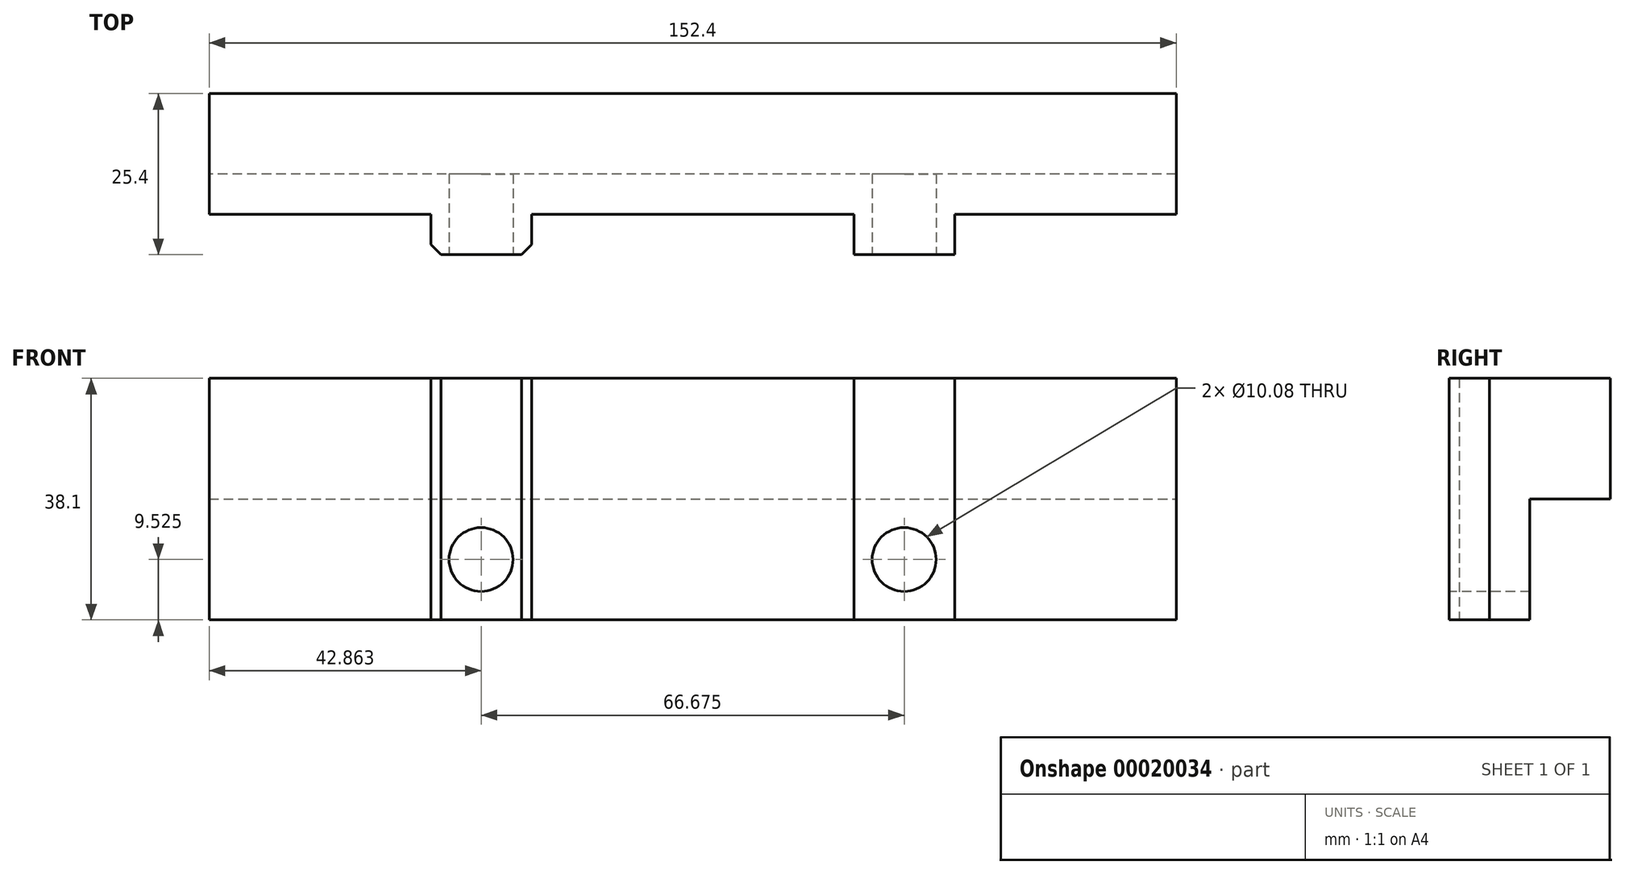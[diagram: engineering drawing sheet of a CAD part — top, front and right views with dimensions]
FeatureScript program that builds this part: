
annotation { "Feature Type Name" : "Feature", "Feature Type Description" : "" }
export const myFeature = defineFeature(function(context is Context, id is Id, definition is map)
    precondition{}
    {
        {
            var Q0;
            Q0=qCreatedBy(makeId("Front.planeOp"),FACE);
            var sketch = newSketch(context, id + "F0", { "sketchPlane" : qUnion([Q0])});
            skLineSegment(sketch, "E0.rect.bottom", {"start": v(76.2, 19.05) * mm, "end": v(-76.2, 19.05) * mm});
            skLineSegment(sketch, "E0.rect.top", {"start": v(76.2, -19.05) * mm, "end": v(-76.2, -19.05) * mm});
            skLineSegment(sketch, "E0.rect.left", {"start": v(76.2, 19.05) * mm, "end": v(76.2, -19.05) * mm});
            skLineSegment(sketch, "E0.rect.right", {"start": v(-76.2, 19.05) * mm, "end": v(-76.2, -19.05) * mm});
            skPoint(sketch, "E0.rect.middle", {"position": v(0, 0) * mm});
            skSolve(sketch);
        }
        {
            var Q0;
            Q0 = qSketchRegion(id + "F0", true);
            extrude(context, id + "F1", {"entities" : qUnion([Q0]), "depth" : 25.4 * mm});
        }
        {
            var Q0;
            Q0=makeQuery(id+"F1.opExtrude","CAP_FACE",FACE,{"disambiguationData":[OSD([sQuery(id+"F0.wireOp",EDGE,"E0.rect.bottom"),sQuery(id+"F0.wireOp",EDGE,"E0.rect.top"),sQuery(id+"F0.wireOp",EDGE,"E0.rect.left"),sQuery(id+"F0.wireOp",EDGE,"E0.rect.right")])],"isStart":false});
            var sketch = newSketch(context, id + "F2", { "sketchPlane" : qUnion([Q0])});
            skLineSegment(sketch, "E1.bottom", {"start": v(-76.2, 19.05) * mm, "end": v(-41.28, 19.05) * mm});
            skLineSegment(sketch, "E1.top", {"start": v(-76.2, -19.05) * mm, "end": v(-41.28, -19.05) * mm});
            skLineSegment(sketch, "E1.left", {"start": v(-76.2, 19.05) * mm, "end": v(-76.2, -19.05) * mm});
            skLineSegment(sketch, "E1.right", {"start": v(-41.28, 19.05) * mm, "end": v(-41.28, -19.05) * mm});
            skLineSegment(sketch, "E2.bottom", {"start": v(-25.4, 19.05) * mm, "end": v(25.4, 19.05) * mm});
            skLineSegment(sketch, "E2.top", {"start": v(-25.4, -19.05) * mm, "end": v(25.4, -19.05) * mm});
            skLineSegment(sketch, "E2.left", {"start": v(-25.4, 19.05) * mm, "end": v(-25.4, -19.05) * mm});
            skLineSegment(sketch, "E2.right", {"start": v(25.4, 19.05) * mm, "end": v(25.4, -19.05) * mm});
            skLineSegment(sketch, "E3.bottom", {"start": v(41.28, 19.05) * mm, "end": v(76.2, 19.05) * mm});
            skLineSegment(sketch, "E3.top", {"start": v(41.28, -19.05) * mm, "end": v(76.2, -19.05) * mm});
            skLineSegment(sketch, "E3.left", {"start": v(41.28, 19.05) * mm, "end": v(41.28, -19.05) * mm});
            skLineSegment(sketch, "E3.right", {"start": v(76.2, 19.05) * mm, "end": v(76.2, -19.05) * mm});
            skSolve(sketch);
        }
        {
            var Q0;
            Q0=makeQuery(id+"F2.imprint","IMPRINT",FACE,{"disambiguationData":[TD([[makeQuery(id+"F2.imprint","IMPRINT",EDGE,{"derivedFrom":sQuery(id+"F2.wireOp",EDGE,"E1.bottom")}),1.0]])]});
            var Q1;
            Q1=makeQuery(id+"F2.imprint","IMPRINT",FACE,{"disambiguationData":[TD([[makeQuery(id+"F2.imprint","IMPRINT",EDGE,{"derivedFrom":sQuery(id+"F2.wireOp",EDGE,"E3.bottom")}),1.0]])]});
            var Q2;
            Q2=makeQuery(id+"F2.imprint","IMPRINT",FACE,{"disambiguationData":[TD([[makeQuery(id+"F2.imprint","IMPRINT",EDGE,{"derivedFrom":sQuery(id+"F2.wireOp",EDGE,"E2.bottom")}),1.0]])]});
            extrude(context, id + "F3", {"entities" : qUnion([Q0, Q1, Q2]), "operationType" : NewBodyOperationType.REMOVE, "oppositeDirection" : true, "depth" : 6.35 * mm});
        }
        {
            var Q0;
            Q0=makeQuery(id+"F3.boolean.opBoolean","COPY",EDGE,{"derivedFrom":makeQuery(id+"F3.opExtrude","CAP_EDGE",EDGE,{"disambiguationData":[OSD([sQuery(id+"F2.wireOp",EDGE,"E1.right")])],"isStart":true})});
            var Q1;
            Q1=makeQuery(id+"F3.boolean.opBoolean","COPY",EDGE,{"derivedFrom":makeQuery(id+"F3.opExtrude","CAP_EDGE",EDGE,{"disambiguationData":[OSD([sQuery(id+"F2.wireOp",EDGE,"E2.left")])],"isStart":true})});
            var Q2;
            Q2=makeQuery(id+"F3.boolean.opBoolean","COPY",EDGE,{"derivedFrom":makeQuery(id+"F3.opExtrude","CAP_EDGE",EDGE,{"disambiguationData":[OSD([sQuery(id+"F2.wireOp",EDGE,"E2.right")])],"isStart":true})});
            var Q3;
            Q3=makeQuery(id+"F3.boolean.opBoolean","COPY",EDGE,{"derivedFrom":makeQuery(id+"F3.opExtrude","CAP_EDGE",EDGE,{"disambiguationData":[OSD([sQuery(id+"F2.wireOp",EDGE,"E3.left")])],"isStart":true})});
            chamfer(context, id + "F4", {"entities" : qUnion([Q0, Q1, Q2, Q3]), "width" : 1.59 * mm, "tangentPropagation" : true});
        }
        {
            var Q0;
            Q0=makeQuery(id+"F1.opExtrude","CAP_FACE",FACE,{"disambiguationData":[OSD([sQuery(id+"F0.wireOp",EDGE,"E0.rect.bottom"),sQuery(id+"F0.wireOp",EDGE,"E0.rect.top"),sQuery(id+"F0.wireOp",EDGE,"E0.rect.left"),sQuery(id+"F0.wireOp",EDGE,"E0.rect.right")])],"isStart":true});
            var sketch = newSketch(context, id + "F5", { "sketchPlane" : qUnion([Q0])});
            skLineSegment(sketch, "E4.bottom", {"start": v(76.2, -19.05) * mm, "end": v(-76.2, -19.05) * mm});
            skLineSegment(sketch, "E4.top", {"start": v(76.2, 0) * mm, "end": v(-76.2, 0) * mm});
            skLineSegment(sketch, "E4.left", {"start": v(76.2, -19.05) * mm, "end": v(76.2, 0) * mm});
            skLineSegment(sketch, "E4.right", {"start": v(-76.2, -19.05) * mm, "end": v(-76.2, 0) * mm});
            skSolve(sketch);
        }
        {
            var Q0;
            Q0 = qSketchRegion(id + "F5", true);
            extrude(context, id + "F6", {"entities" : qUnion([Q0]), "operationType" : NewBodyOperationType.REMOVE, "oppositeDirection" : true, "depth" : 12.7 * mm});
        }
        {
            var Q0;
            {var subQ0=sQuery(id+"F0.wireOp",EDGE,"E0.rect.bottom");var subQ1=sQuery(id+"F0.wireOp",EDGE,"E0.rect.top");Q0=makeQuery(id+"F3.boolean.opBoolean","SPLIT",FACE,{"disambiguationData":[TD([makeQuery(id+"F3.opExtrude","SWEPT_FACE",FACE,{"disambiguationData":[OSD([sQuery(id+"F2.wireOp",EDGE,"E2.right")])]})])],"derivedFrom":makeQuery(id+"F1.opExtrude","CAP_FACE",FACE,{"disambiguationData":[OSD([subQ0,subQ1,sQuery(id+"F0.wireOp",EDGE,"E0.rect.left"),sQuery(id+"F0.wireOp",EDGE,"E0.rect.right")])],"isStart":false})});}
            var sketch = newSketch(context, id + "F7", { "sketchPlane" : qUnion([Q0])});
            skPoint(sketch, "E5", {"position": v(33.34, -9.53) * mm});
            skPoint(sketch, "E6", {"position": v(-33.34, -9.53) * mm});
            skSolve(sketch);
        }
        {
            var Q0;
            Q0=sQuery(id+"F7.wireOp",VERTEX,"E5");
            var Q1;
            Q1=sQuery(id+"F7.wireOp",VERTEX,"E6");
            var Q2;
            Q2=makeQuery(id+"F1.opExtrude","SWEPT_BODY",BODY,{"disambiguationData":[OSD([sQuery(id+"F0.wireOp",EDGE,"E0.rect.bottom"),sQuery(id+"F0.wireOp",EDGE,"E0.rect.top"),sQuery(id+"F0.wireOp",EDGE,"E0.rect.left"),sQuery(id+"F0.wireOp",EDGE,"E0.rect.right")])]});
            hole(context, id + "F8", {"style" : HoleStyle.SIMPLE, "holeDiameter" : 10.08 * mm, "endStyle" : HoleEndStyle.THROUGH, "locations" : qUnion([Q0, Q1]), "scope" : qUnion([Q2])});
        }
    });
